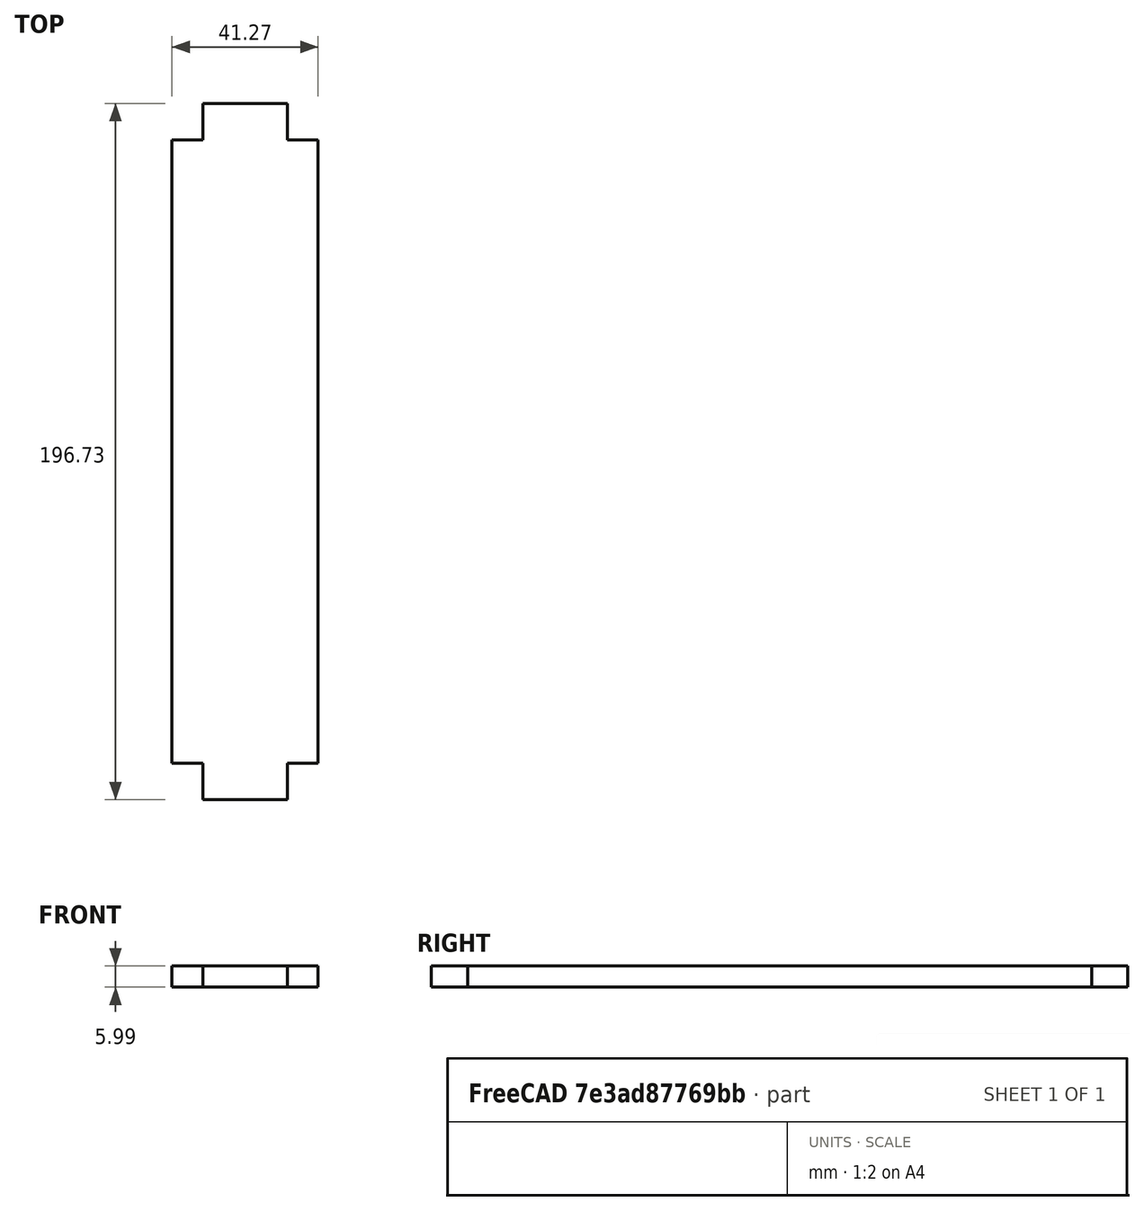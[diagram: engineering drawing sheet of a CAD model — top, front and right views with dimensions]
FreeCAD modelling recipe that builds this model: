
FCSTD DOCUMENT  (FreeCAD 0.19R24267 (Git))
Label: Inv1-P7
License: All rights reserved
LicenseURL: http://en.wikipedia.org/wiki/All_rights_reserved
objects: TechDraw::DrawViewDimension×9, TechDraw::DrawProjGroupItem×2, TechDraw::DrawHatch×2, TechDraw::DrawViewAnnotation×2, Sketcher::SketchObject×1, Part::Extrusion×1, TechDraw::DrawSVGTemplate×1, TechDraw::DrawProjGroup×1, TechDraw::DrawPage×1
note: 2 computed .brp shape members not serialized (recipe doc carries the construction recipe); baked Part::Feature solids carry a one-line shape summary decoded from their .brp

FEATURE [Sketcher::SketchObject] Sketch
  FullyConstrained = false
  sketch-geometry (12):
    g0: LineSegment StartX=0.00742828 StartY=-10.6387 StartZ=0 EndX=8.71963 EndY=-10.6387 EndZ=0
    g1: LineSegment StartX=8.71963 StartY=-10.6387 StartZ=0 EndX=8.71963 EndY=-0.402466 EndZ=0
    g2: LineSegment StartX=8.71963 StartY=-197.125 StartZ=0 EndX=8.71963 EndY=-186.889 EndZ=0
    g3: LineSegment StartX=8.71963 StartY=-186.889 StartZ=0 EndX=0.00742828 EndY=-186.889 EndZ=0
    g4: LineSegment StartX=32.5702 StartY=-197.125 StartZ=0 EndX=32.5702 EndY=-186.889 EndZ=0
    g5: LineSegment StartX=32.5702 StartY=-186.889 StartZ=0 EndX=41.2824 EndY=-186.889 EndZ=0
    g6: LineSegment StartX=32.5702 StartY=-0.402466 StartZ=0 EndX=32.5702 EndY=-10.6387 EndZ=0
    g7: LineSegment StartX=32.5702 StartY=-10.6387 StartZ=0 EndX=41.2824 EndY=-10.6387 EndZ=0
    g8: LineSegment StartX=0.00742828 StartY=-10.6387 StartZ=0 EndX=0.00742828 EndY=-186.889 EndZ=0
    g9: LineSegment StartX=41.2824 StartY=-10.6387 StartZ=0 EndX=41.2824 EndY=-186.889 EndZ=0
    g10: LineSegment StartX=32.5702 StartY=-197.125 StartZ=0 EndX=8.71963 EndY=-197.125 EndZ=0
    g11: LineSegment StartX=8.71963 StartY=-0.402466 StartZ=0 EndX=32.5702 EndY=-0.402466 EndZ=0
  constraints (34):
    c: Coincident(g0,g1)
    c: Horizontal(g0)
    c: Vertical(g1)
    c: Distance(g1) = 10.2362
    c: Distance(g0) = 8.7122
    c: Coincident(g2,g3)
    c: Horizontal(g3)
    c: Vertical(g2)
    c: Coincident(g4,g5)
    c: Horizontal(g5)
    c: Vertical(g4)
    c: Coincident(g6,g7)
    c: Horizontal(g7)
    c: Vertical(g6)
    c: Equal(g7,g0)
    c: Equal(g0,g5)
    c: Equal(g6,g1)
    c: Equal(g1,g2)
    c: Equal(g1,g4)
    c: Equal(g3,g0)
    c: Coincident(g8,g0)
    c: Coincident(g8,g3)
    c: Vertical(g8)
    c: Coincident(g9,g7)
    c: Coincident(g9,g5)
    c: Vertical(g9)
    c: Horizontal(g10)
    c: Coincident(g10,g4)
    c: Coincident(g2,g10)
    c: Coincident(g11,g1)
    c: Coincident(g11,g6)
    c: Horizontal(g11)
    c: Distance(g6,g10) = 196.723
    c: Distance(g3,g9) = 41.275
FEATURE [Part::Extrusion] Extrude
  Base = -> Sketch
  Dir = (0,0,1)
  DirMode = 2
  FaceMakerClass = Part::FaceMakerBullseye
  LengthFwd = 5.9944
  LengthRev = 0
  Solid = true
  Symmetric = false
FEATURE [TechDraw::DrawSVGTemplate] Template
  Height = 215.9
  Orientation = 1
  Width = 279.4
FEATURE [TechDraw::DrawProjGroupItem] ProjItem  label="Front"
  CoarseView = false
  Direction = (0,0,1)
  Focus = 100
  HardHidden = false
  IsoCount = 0
  IsoHidden = false
  IsoVisible = false
  LockPosition = true
  Perspective = false
  Rotation = 0
  RotationVector = (1,0,0)
  Scale = 0.5
  ScaleType = 2
  SeamHidden = false
  SeamVisible = true
  SmoothHidden = false
  SmoothVisible = true
  Source = -> [Extrude]
  Type = 0
  X = 0
  XDirection = (1,0,0)
  Y = 0
FEATURE [TechDraw::DrawProjGroupItem] ProjItem001  label="Left"
  CoarseView = false
  Direction = (-1,0,1e-16)
  Focus = 100
  HardHidden = false
  IsoCount = 0
  IsoHidden = false
  IsoVisible = false
  LockPosition = false
  Perspective = false
  Rotation = 0
  RotationVector = (1,0,0)
  Scale = 0.5
  ScaleType = 2
  SeamHidden = false
  SeamVisible = true
  SmoothHidden = false
  SmoothVisible = true
  Source = -> [Extrude]
  Type = 1
  X = 49.3488
  XDirection = (1e-16,0,1)
  Y = 0
FEATURE [TechDraw::DrawProjGroup] ProjGroup
  Anchor = -> ProjItem
  AutoDistribute = true
  LockPosition = false
  ProjectionType = 0
  Rotation = 0
  Scale = 0.5
  ScaleType = 0
  Source = -> [Extrude]
  Views = -> [ProjItem,ProjItem001]
  X = 139.7
  Y = 107.95
  spacingX = 15.0114
  spacingY = 15.0114
FEATURE [TechDraw::DrawHatch] Hatch  label="HatchF0"
  HatchPattern = <path>
  Source = -> ProjItem [Face0]
FEATURE [TechDraw::DrawHatch] Hatch001  label="Hatch001F2"
  HatchPattern = <path>
  Source = -> ProjItem001 [Face2,Face1,Face3]
FEATURE [TechDraw::DrawViewAnnotation] Annotation
  Font = osifont
  LineSpace = 80
  LockPosition = false
  MaxWidth = -1
  Rotation = 0
  ScaleType = 0
  Text = Figure S1 (Inverted 1) | Panel 7 [camera port top] | Quantity: 1
  TextSize = 5.0038
  TextStyle = 0
  X = 36.7424
  Y = 195.58
FEATURE [TechDraw::DrawViewAnnotation] Annotation002
  Font = osifont
  LineSpace = 80
  LockPosition = false
  MaxWidth = -1
  Rotation = 0
  ScaleType = 0
  Text = Units: Inches
  TextSize = 5.0038
  TextStyle = 0
  X = 259.08
  Y = 5.08
FEATURE [TechDraw::DrawViewDimension] Dimension
  Arbitrary = false
  ArbitraryTolerances = false
  EqualTolerance = true
  FormatSpec = %.3f
  FormatSpecOverTolerance = %+.3f
  FormatSpecUnderTolerance = %+.3f
  Inverted = false
  LockPosition = false
  MeasureType = 1
  OverTolerance = 0
  References2D = -> [ProjItem001]
  Rotation = 0
  ScaleType = 0
  TheoreticalExact = false
  Type = 1
  UnderTolerance = 0
  X = 24.1882
  Y = 37.5037
FEATURE [TechDraw::DrawViewDimension] Dimension001
  Arbitrary = false
  ArbitraryTolerances = false
  EqualTolerance = true
  FormatSpec = %.3f
  FormatSpecOverTolerance = %+.3f
  FormatSpecUnderTolerance = %+.3f
  Inverted = false
  LockPosition = false
  MeasureType = 1
  OverTolerance = 0
  References2D = -> [ProjItem]
  Rotation = 0
  ScaleType = 0
  TheoreticalExact = false
  Type = 2
  UnderTolerance = 0
  X = 23.508
  Y = 1.94618
FEATURE [TechDraw::DrawViewDimension] Dimension002
  Arbitrary = false
  ArbitraryTolerances = false
  EqualTolerance = true
  FormatSpec = %.3f
  FormatSpecOverTolerance = %+.3f
  FormatSpecUnderTolerance = %+.3f
  Inverted = false
  LockPosition = false
  MeasureType = 1
  OverTolerance = 0
  References2D = -> [ProjItem]
  Rotation = 0
  ScaleType = 0
  TheoreticalExact = false
  Type = 1
  UnderTolerance = 0
  X = -0.860611
  Y = -81.5945
FEATURE [TechDraw::DrawViewDimension] Dimension003
  Arbitrary = false
  ArbitraryTolerances = false
  EqualTolerance = true
  FormatSpec = %.3f
  FormatSpecOverTolerance = %+.3f
  FormatSpecUnderTolerance = %+.3f
  Inverted = false
  LockPosition = false
  MeasureType = 1
  OverTolerance = 0
  References2D = -> [ProjItem]
  Rotation = 0
  ScaleType = 0
  TheoreticalExact = false
  Type = 2
  UnderTolerance = 0
  X = -25.392
  Y = 23.1964
FEATURE [TechDraw::DrawViewDimension] Dimension004
  Arbitrary = false
  ArbitraryTolerances = false
  EqualTolerance = true
  FormatSpec = %.3f
  FormatSpecOverTolerance = %+.3f
  FormatSpecUnderTolerance = %+.3f
  Inverted = false
  LockPosition = false
  MeasureType = 1
  OverTolerance = 0
  References2D = -> [ProjItem]
  Rotation = 0
  ScaleType = 0
  TheoreticalExact = false
  Type = 2
  UnderTolerance = 0
  X = -25.2701
  Y = -18.6651
FEATURE [TechDraw::DrawViewDimension] Dimension005
  Arbitrary = false
  ArbitraryTolerances = false
  EqualTolerance = true
  FormatSpec = %.3f
  FormatSpecOverTolerance = %+.3f
  FormatSpecUnderTolerance = %+.3f
  Inverted = false
  LockPosition = false
  MeasureType = 1
  OverTolerance = 0
  References2D = -> [ProjItem]
  Rotation = 0
  ScaleType = 0
  TheoreticalExact = false
  Type = 1
  UnderTolerance = 0
  X = -23.3688
  Y = 77.6913
FEATURE [TechDraw::DrawViewDimension] Dimension006
  Arbitrary = false
  ArbitraryTolerances = false
  EqualTolerance = true
  FormatSpec = %.3f
  FormatSpecOverTolerance = %+.3f
  FormatSpecUnderTolerance = %+.3f
  Inverted = false
  LockPosition = false
  MeasureType = 1
  OverTolerance = 0
  References2D = -> [ProjItem]
  Rotation = 0
  ScaleType = 0
  TheoreticalExact = false
  Type = 1
  UnderTolerance = 0
  X = 24.0033
  Y = 73.8843
FEATURE [TechDraw::DrawViewDimension] Dimension007
  Arbitrary = false
  ArbitraryTolerances = false
  EqualTolerance = true
  FormatSpec = %.3f
  FormatSpecOverTolerance = %+.3f
  FormatSpecUnderTolerance = %+.3f
  Inverted = false
  LockPosition = false
  MeasureType = 1
  OverTolerance = 0
  References2D = -> [ProjItem]
  Rotation = 0
  ScaleType = 0
  TheoreticalExact = false
  Type = 1
  UnderTolerance = 0
  X = -30.1368
  Y = -67.3277
FEATURE [TechDraw::DrawViewDimension] Dimension008
  Arbitrary = false
  ArbitraryTolerances = false
  EqualTolerance = true
  FormatSpec = %.3f
  FormatSpecOverTolerance = %+.3f
  FormatSpecUnderTolerance = %+.3f
  Inverted = false
  LockPosition = false
  MeasureType = 1
  OverTolerance = 0
  References2D = -> [ProjItem]
  Rotation = 0
  ScaleType = 0
  TheoreticalExact = false
  Type = 1
  UnderTolerance = 0
  X = 22.0395
  Y = -62.0402
FEATURE [TechDraw::DrawPage] Page
  KeepUpdated = true
  NextBalloonIndex = 1
  ProjectionType = 0
  Template = -> Template
  Views = -> [ProjGroup,Annotation,Annotation002,Dimension,Dimension001,Dimension002,Dimension003,Dimension004,Dimension005,Dimension006,Dimension007,Dimension008]
note: 2 file-system paths scrubbed to <path> (originals preserved in the JSON sidecar)
